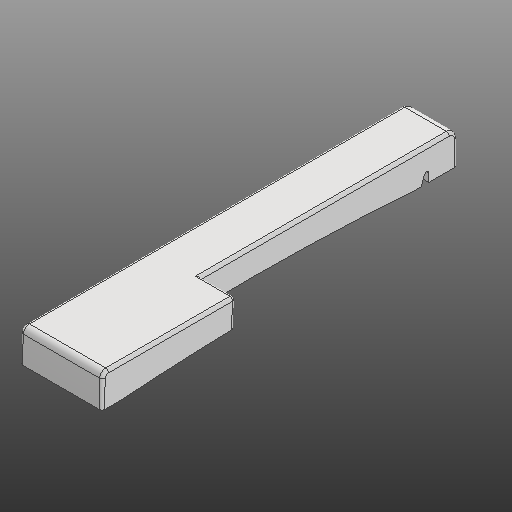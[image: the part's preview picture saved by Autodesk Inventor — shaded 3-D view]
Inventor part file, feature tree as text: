
AUTODESK INVENTOR PART (.ipt)
format: ipt  version: 2020 (Build 240168000, 168)  size: 316,416 bytes
history: native  units: in
note: dims shown in document units (in); Inventor stores cm internally (conversion verified against a paired STEP export)
features: extrude x4, other x3, fillet x2
ambient origin geometry x8: Origin, YZ Plane, XZ Plane, XY Plane, X Axis, Y Axis, Z Axis, Center Point
bodies: Solid1 (feature_tree)
feature tree (9):
  other  "Slot Start Plane"
  other  "Key Profile"
  extrude  "Upper (u)"  TaperAngle=0.0deg  [1 undecoded]
  extrude  "Lower (d)"  TaperAngle=0.0deg  [1 undecoded]
  extrude  "Protrusion Cutout"  Depth=0.0591in
  fillet  "Front Fillet"  Radius=0.1374in
  extrude  "Slot"  [1 undecoded]
  fillet  "Edge Softening"  Radius=0.0787in
  other  "Slot Sketch"
note: 3 required parameter values undecoded (feature->parameter linkage not recoverable at this tier; creation-order binding heuristic only, values carry confidence <= 0.55)
